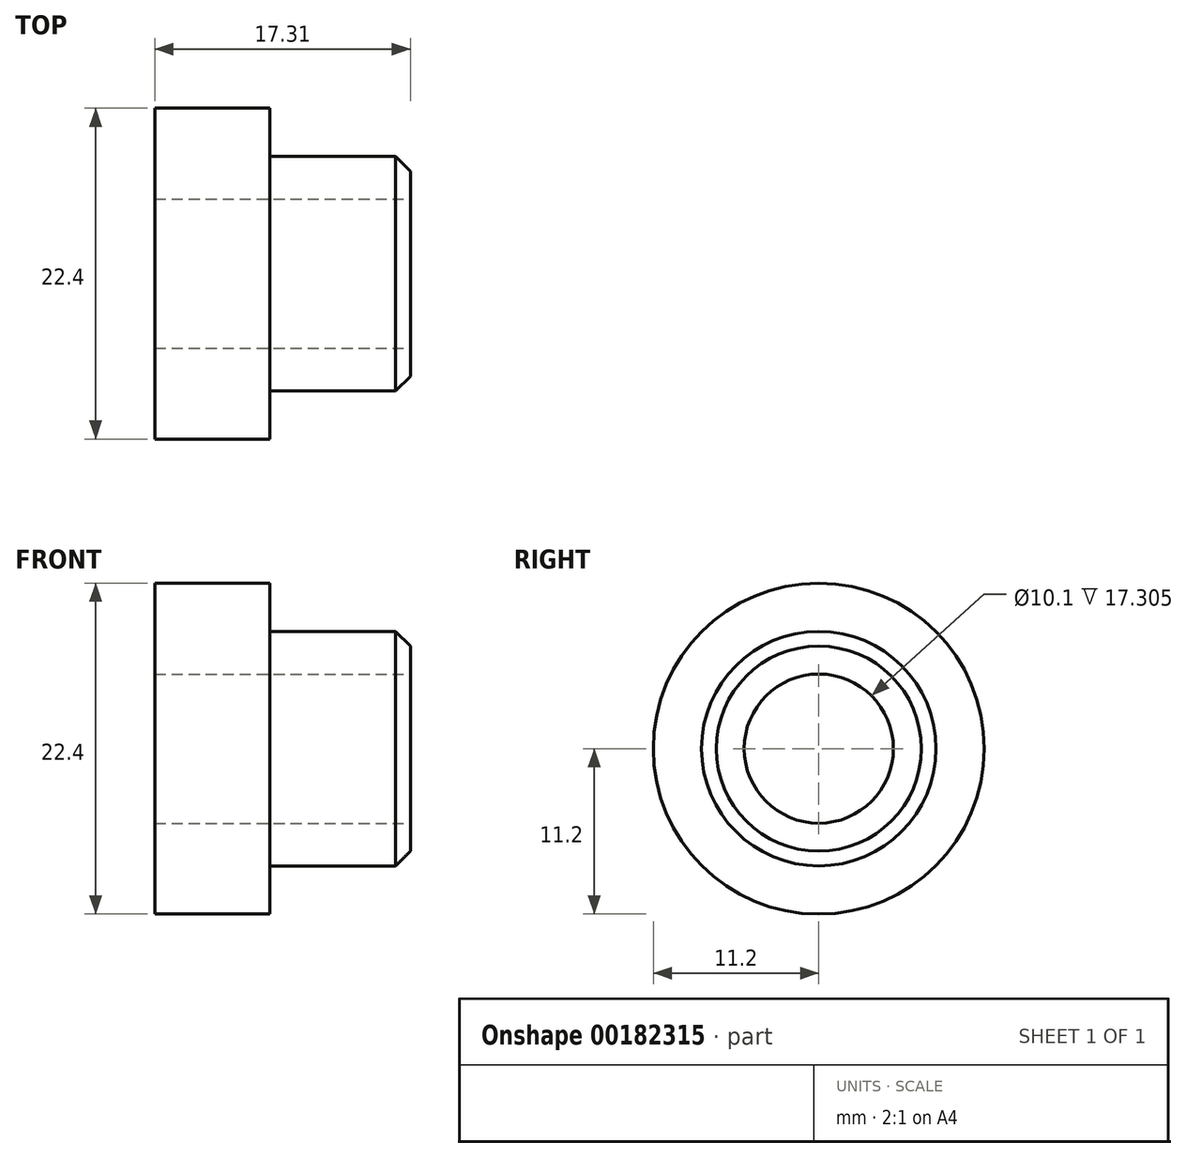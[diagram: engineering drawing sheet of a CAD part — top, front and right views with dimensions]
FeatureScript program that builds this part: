
annotation { "Feature Type Name" : "Feature", "Feature Type Description" : "" }
export const myFeature = defineFeature(function(context is Context, id is Id, definition is map)
    precondition{}
    {
        {
            var Q0;
            Q0=qCreatedBy(makeId("Right.planeOp"),FACE);
            var sketch = newSketch(context, id + "F0", { "sketchPlane" : qUnion([Q0])});
            skCircle(sketch, "E0", {"center": v(0, 0) * mm, "radius": 11.2 * mm});
            skSolve(sketch);
        }
        {
            var Q0;
            Q0=makeQuery(id+"F0.imprint","IMPRINT",FACE,{"disambiguationData":[TD([[makeQuery(id+"F0.imprint","IMPRINT",EDGE,{"derivedFrom":sQuery(id+"F0.wireOp",EDGE,"E0")}),1.0]])]});
            extrude(context, id + "F1", {"entities" : qUnion([Q0]), "depth" : 7.78 * mm});
        }
        {
            var Q0;
            Q0=makeQuery(id+"F1.opExtrude","CAP_FACE",FACE,{"disambiguationData":[OSD([sQuery(id+"F0.wireOp",EDGE,"E0")])],"isStart":false});
            var sketch = newSketch(context, id + "F2", { "sketchPlane" : qUnion([Q0])});
            skCircle(sketch, "E1", {"center": v(0, 0) * mm, "radius": 7.94 * mm});
            skSolve(sketch);
        }
        {
            var Q0;
            Q0=qSketchRegion(id+"F2",true);
            extrude(context, id + "F3", {"entities" : qUnion([Q0]), "operationType" : NewBodyOperationType.ADD, "depth" : 9.52 * mm});
        }
        {
            var Q0;
            Q0=makeQuery(id+"F3.opExtrude","CAP_FACE",FACE,{"disambiguationData":[OSD([sQuery(id+"F2.wireOp",EDGE,"E1")])],"isStart":false});
            var sketch = newSketch(context, id + "F4", { "sketchPlane" : qUnion([Q0])});
            skCircle(sketch, "E2", {"center": v(0, 0) * mm, "radius": 5.08 * mm});
            skSolve(sketch);
        }
        {
            var Q0;
            Q0=sQuery(id+"F4.wireOp",VERTEX,"E2.center");
            var Q1;
            Q1=makeQuery(id+"F1.opExtrude","SWEPT_BODY",BODY,{"disambiguationData":[OSD([sQuery(id+"F0.wireOp",EDGE,"E0")])]});
            hole(context, id + "F5", {"style" : HoleStyle.SIMPLE, "endStyle" : HoleEndStyle.THROUGH, "holeDiameter" : 10.1 * mm, "locations" : qUnion([Q0]), "scope" : qUnion([Q1]), "isTappedThrough" : true});
        }
        {
            var Q0;
            Q0=makeQuery(id+"F3.opExtrude","CAP_EDGE",EDGE,{"disambiguationData":[OSD([sQuery(id+"F2.wireOp",EDGE,"E1")])],"isStart":false});
            chamfer(context, id + "F6", {"entities" : qUnion([Q0]), "chamferType" : ChamferType.OFFSET_ANGLE, "width" : 1 * mm, "oppositeDirection" : false, "angle" : 45 * degree, "tangentPropagation" : true});
        }
    });
